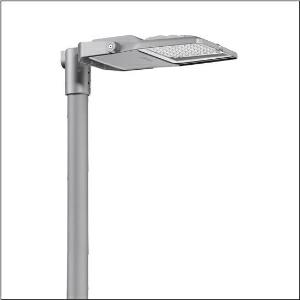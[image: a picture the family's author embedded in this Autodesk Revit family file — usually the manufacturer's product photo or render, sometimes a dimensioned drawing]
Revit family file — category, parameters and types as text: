
# Revit family: floodlight_fl_21_mini___pl61_5xa7776c2c3a_9e20
name_source: partatom
category: Lighting Fixtures
units: mm (PartAtom-declared; Revit-internal decimal feet)

## family parameters
Cut with Voids When Loaded = No
Host = Face
Light Source = No
Part Type = Normal
Room Calculation Point = No
Round Connector Dimension = Use Diameter
Shared = No

## types (1)
- --- (1 x LED, 11960 lm, 89 W, 3000K)
    Apparent Load = 89 VA
    CIE Flux Codes = 33 65 98 100 100
    Color Rendering = 70
    Color Temperature = 3000K
    Default Elevation = 1800 mm
    Description = Floodlight FL 21 mini, floodlight, primary light control with lens, of PMMA, primary optical cover: protective disc, of toughened safety glass, transparent, light distribution: PL61, light emission: direct distribution, installation type: surface-mounted, LED, High Power LED, rated luminous flux: 11.960lm, luminous efficacy: 134lm/W, light colour: 730, colour temperature: 3000K, control: flexible luminous flux parameterisation, time-dependent luminous flux control, constant luminous flux control, overheat protection, pre-setting: logarithmic dimming characteristic, with terminal, 6-pole, mains connection: 220..240V, AC, 50/60Hz, start of lifetime: 89W, end of service life: 94W, reduction: 43W, luminaire housing, of diecast aluminium, powder-coated, Siteco® metallic grey (DB 702S), corrosivity category C5 mid according to DIN EN ISO 12944, sealing non-destructively replaceable, please order mast flange separately, mast bracket, of steel, galvanised, powder-coated, Siteco® metallic grey (DB 702S), Smart Interface below and above, protection rating (complete): IP66, insulation class (complete): insulation class II (safety insulation), certification: CE, ENEC, VDE, protection symbol: D, impact resistance: IK08, permissible operating ambient temperature: -40..+40°C, permissible operating ambient temperature for outdoor applications: -40..+50°C, standard: DIN EN 12944, LABS conformity tested according to VDMA 24364:2018-05, packaging unit: 1 piece

Light Distribution: PL61
    Height = 70 mm
    Lamp = 1 x LED
    Lamp Light Flux = 11960 lm
    Lamp Power = 89 W
    Lamp count = 1
    Length = 485 mm
    Luminous efficacy = 134 lm/W
    Manufacturer = Siteco
    ModVariant = No
    Model = 5XA7776C2C3A
    Number of Poles = 1
    OnlyDefault = Yes
    Power Factor = 1
    Product Name = Floodlight FL 21 mini | PL61
    Product group = floodlight | pylon annexe
    ProductGroupID = 6200
    Protection Class = Protection class II
    Protection Degree = IP 66
    RLX_Detail_Level = 1
    RLX_Emergency_Light_Flux = 0 lm
    RLX_Emergency_Type = 0
    RLX_Emergency_Type_DB = No
    RlxData = <blob elided: 100921 chars, md5=3da7737e>
    Socket = socket
    Standby Power = 0 W
    System Light Flux = 11960 lm
    System Power = 89 W
    Type Comments = factory setting: luminous flux: 100 % | dim-lin: 254 | 456 mA
    Type Image = l_1007125.jpg
    URL = http://relux.com
    VarID = @adj_143107
    Voltage = 0 V
    Weight = 0.00 kg
    Width = 337 mm

## geometry (parser evidence)
native form markers: Blend x4, Sweep x12
no freeform markers — native parametric forms only
